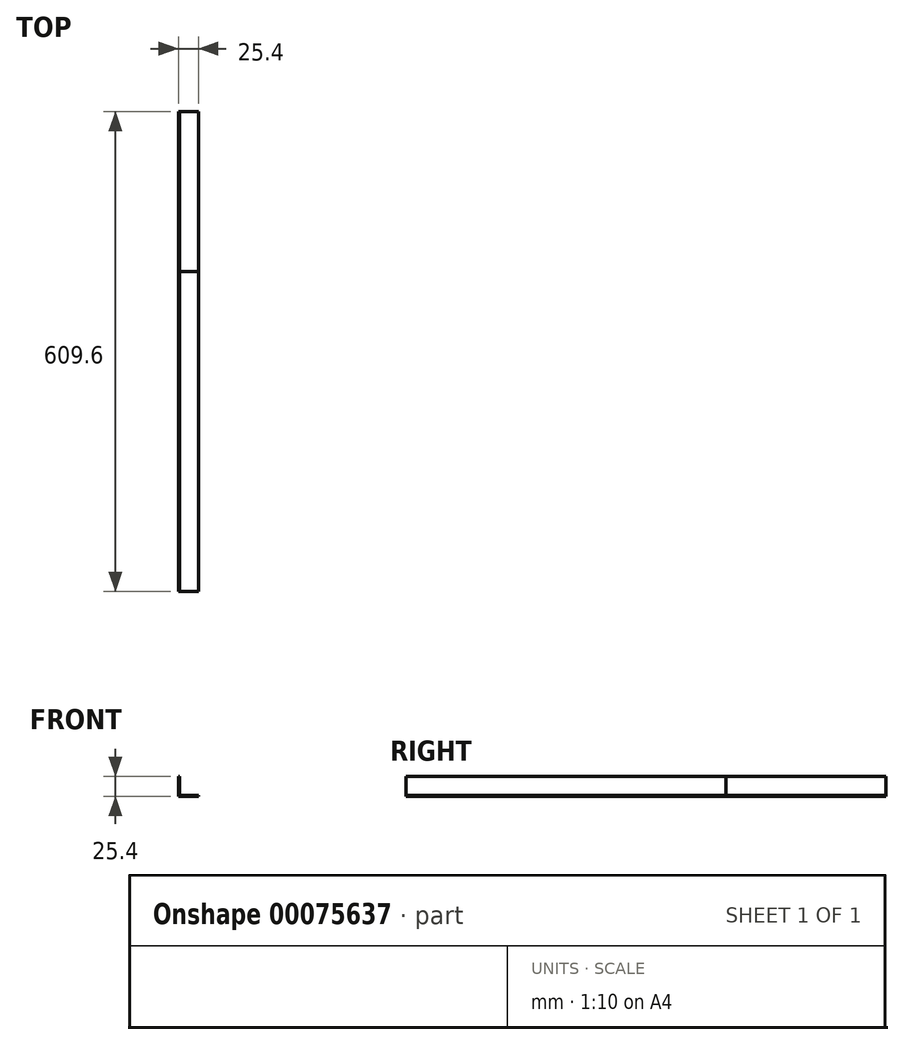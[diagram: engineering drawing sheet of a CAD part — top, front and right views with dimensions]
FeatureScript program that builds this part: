
annotation { "Feature Type Name" : "Feature", "Feature Type Description" : "" }
export const myFeature = defineFeature(function(context is Context, id is Id, definition is map)
    precondition{}
    {
        {
            var Q0;
            Q0=qCreatedBy(makeId("Front.planeOp"),FACE);
            var sketch = newSketch(context, id + "F0", { "sketchPlane" : qUnion([Q0])});
            skLineSegment(sketch, "E0", {"start": v(0, 0) * mm, "end": v(0, 25.4) * mm});
            skLineSegment(sketch, "E1", {"start": v(0, 25.4) * mm, "end": v(1.59, 25.4) * mm});
            skLineSegment(sketch, "E2", {"start": v(1.59, 25.4) * mm, "end": v(1.59, 1.59) * mm});
            skLineSegment(sketch, "E3", {"start": v(1.59, 1.59) * mm, "end": v(25.4, 1.59) * mm});
            skLineSegment(sketch, "E4", {"start": v(25.4, 1.59) * mm, "end": v(25.4, 0) * mm});
            skLineSegment(sketch, "E5", {"start": v(25.4, 0) * mm, "end": v(0, 0) * mm});
            skSolve(sketch);
        }
        {
            var Q0;
            Q0=makeQuery(id+"F0.imprint","IMPRINT",FACE,{"disambiguationData":[TD([[makeQuery(id+"F0.imprint","IMPRINT",EDGE,{"derivedFrom":sQuery(id+"F0.wireOp",EDGE,"E0")}),-1.0]])]});
            extrude(context, id + "F1", {"entities" : qUnion([Q0]), "depth" : 203.2 * mm});
        }
        {
            var Q0;
            Q0 = qSketchRegion(id + "F0", true);
            extrude(context, id + "F2", {"entities" : qUnion([Q0]), "depth" : 609.6 * mm});
        }
    });
